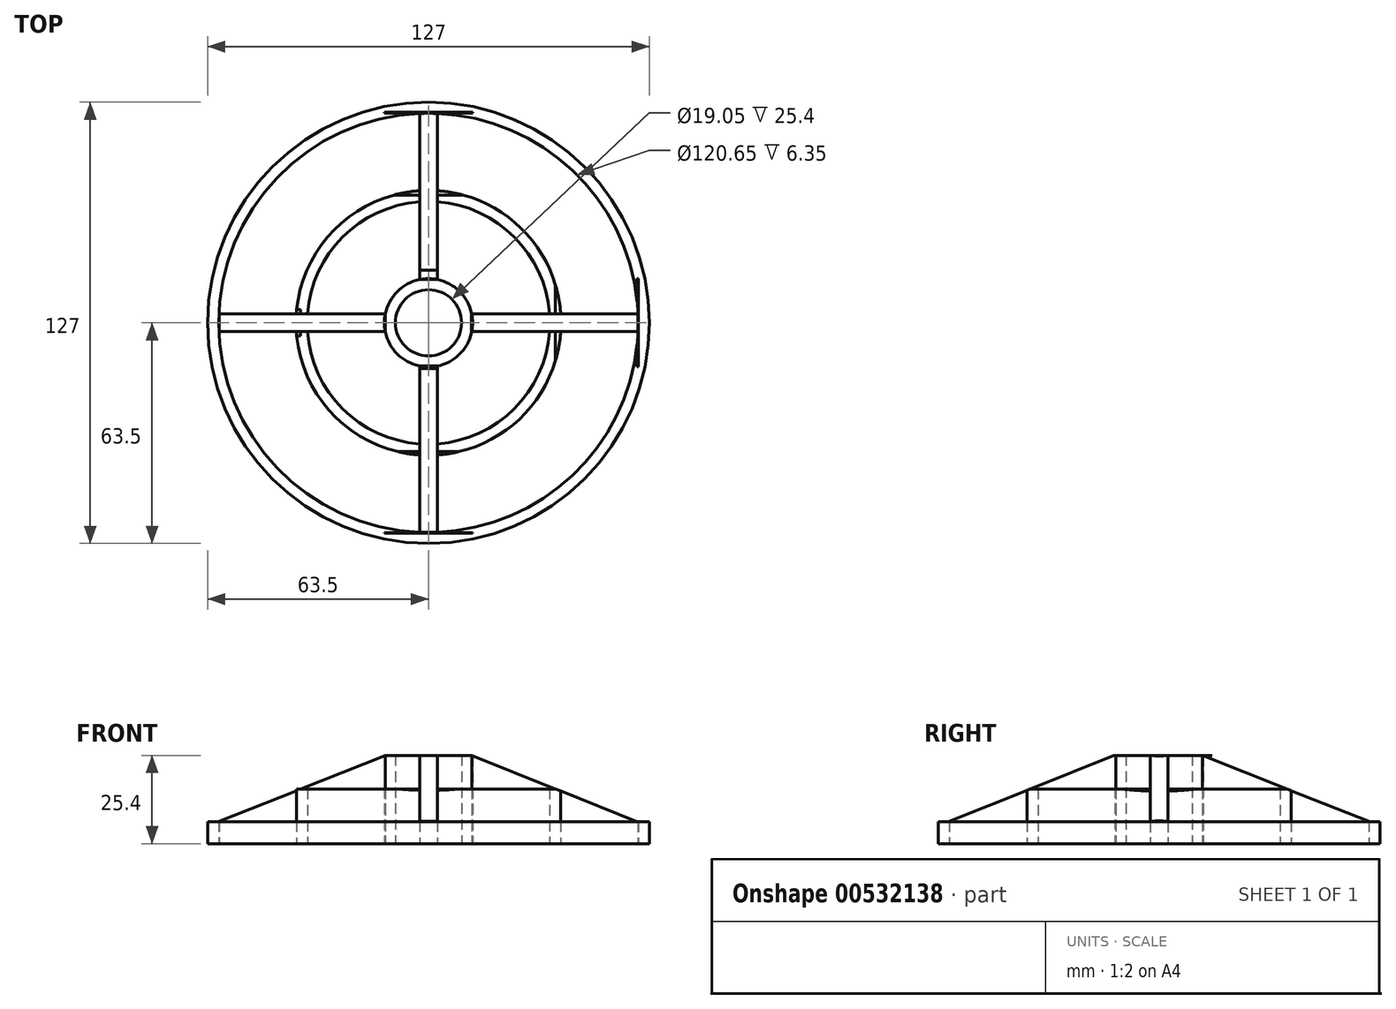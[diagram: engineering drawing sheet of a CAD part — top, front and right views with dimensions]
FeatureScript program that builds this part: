
annotation { "Feature Type Name" : "Feature", "Feature Type Description" : "" }
export const myFeature = defineFeature(function(context is Context, id is Id, definition is map)
    precondition{}
    {
        {
            var Q0;
            Q0=qCreatedBy(makeId("Top.planeOp"),FACE);
            var sketch = newSketch(context, id + "F0", { "sketchPlane" : qUnion([Q0])});
            skCircle(sketch, "E0", {"center": v(0, 0) * mm, "radius": 63.5 * mm});
            skCircle(sketch, "E1", {"center": v(0, 0) * mm, "radius": 38.1 * mm});
            skCircle(sketch, "E2", {"center": v(0, 0) * mm, "radius": 12.7 * mm});
            skLineSegment(sketch, "E3", {"start": v(-2.57, 63.45) * mm, "end": v(-2.57, 12.44) * mm});
            skLineSegment(sketch, "E4", {"start": v(2.51, 63.45) * mm, "end": v(2.51, 12.45) * mm});
            skLineSegment(sketch, "E5", {"start": v(-12.44, 2.55) * mm, "end": v(-63.45, 2.55) * mm});
            skLineSegment(sketch, "E6", {"start": v(-12.45, -2.53) * mm, "end": v(-63.45, -2.53) * mm});
            skLineSegment(sketch, "E7", {"start": v(2.51, -12.45) * mm, "end": v(2.51, -63.45) * mm});
            skLineSegment(sketch, "E8", {"start": v(-2.57, -12.44) * mm, "end": v(-2.57, -63.45) * mm});
            skLineSegment(sketch, "E9", {"start": v(12.44, 2.55) * mm, "end": v(63.45, 2.55) * mm});
            skLineSegment(sketch, "E10", {"start": v(12.45, -2.53) * mm, "end": v(63.45, -2.53) * mm});
            skCircle(sketch, "E11", {"center": v(0, 0) * mm, "radius": 60.33 * mm});
            skCircle(sketch, "E12", {"center": v(0, 0) * mm, "radius": 34.93 * mm});
            skCircle(sketch, "E13", {"center": v(0, 0) * mm, "radius": 9.53 * mm});
            skLineSegment(sketch, "E14", {"start": v(-60.21, 2.55) * mm, "end": v(-60.21, -2.53) * mm});
            skLineSegment(sketch, "E15", {"start": v(-12.44, 2.55) * mm, "end": v(-12.45, -2.53) * mm});
            skLineSegment(sketch, "E16", {"start": v(12.44, 2.55) * mm, "end": v(12.45, -2.53) * mm});
            skLineSegment(sketch, "E17", {"start": v(63.45, 2.55) * mm, "end": v(63.45, -2.53) * mm});
            skLineSegment(sketch, "E18", {"start": v(-2.57, 63.45) * mm, "end": v(2.51, 63.45) * mm});
            skLineSegment(sketch, "E19", {"start": v(2.51, 12.45) * mm, "end": v(-2.57, 12.44) * mm});
            skLineSegment(sketch, "E20", {"start": v(-2.57, -12.44) * mm, "end": v(2.51, -12.45) * mm});
            skLineSegment(sketch, "E21", {"start": v(2.51, -63.45) * mm, "end": v(-2.57, -63.45) * mm});
            skSolve(sketch);
        }
        {
            var Q0;
            Q0=qSketchRegion(id+"F0",true);
            extrude(context, id + "F1", {"entities" : qUnion([Q0]), "depth" : 6.35 * mm, "offsetDistance" : 25.4 * mm});
        }
        {
            var Q0;
            {var subQ0=sQuery(id+"F0.wireOp",EDGE,"E3");var subQ1=sQuery(id+"F0.wireOp",EDGE,"E1");var subQ2=makeQuery(id+"F0.imprint","INTERSECT",VERTEX,{"derivedFrom":[subQ1,subQ0]});Q0=makeQuery(id+"F0.imprint","IMPRINT",FACE,{"disambiguationData":[TD([[makeQuery(id+"F0.imprint","IMPRINT",EDGE,{"disambiguationData":[TD([[subQ2,-1.0]])],"derivedFrom":subQ1}),1.0]])]});}
            var Q1;
            {var subQ0=sQuery(id+"F0.wireOp",EDGE,"E4");var subQ1=sQuery(id+"F0.wireOp",EDGE,"E1");var subQ2=makeQuery(id+"F0.imprint","INTERSECT",VERTEX,{"derivedFrom":[subQ1,subQ0]});Q1=makeQuery(id+"F0.imprint","IMPRINT",FACE,{"disambiguationData":[TD([[makeQuery(id+"F0.imprint","IMPRINT",EDGE,{"disambiguationData":[TD([[subQ2,1.0]])],"derivedFrom":subQ1}),1.0]])]});}
            var Q2;
            {var subQ0=sQuery(id+"F0.wireOp",EDGE,"E7");var subQ1=sQuery(id+"F0.wireOp",EDGE,"E1");var subQ2=makeQuery(id+"F0.imprint","INTERSECT",VERTEX,{"derivedFrom":[subQ1,subQ0]});Q2=makeQuery(id+"F0.imprint","IMPRINT",FACE,{"disambiguationData":[TD([[makeQuery(id+"F0.imprint","IMPRINT",EDGE,{"disambiguationData":[TD([[subQ2,-1.0]])],"derivedFrom":subQ1}),1.0]])]});}
            var Q3;
            {var subQ0=sQuery(id+"F0.wireOp",EDGE,"E6");var subQ1=sQuery(id+"F0.wireOp",EDGE,"E1");var subQ2=makeQuery(id+"F0.imprint","INTERSECT",VERTEX,{"derivedFrom":[subQ1,subQ0]});Q3=makeQuery(id+"F0.imprint","IMPRINT",FACE,{"disambiguationData":[TD([[makeQuery(id+"F0.imprint","IMPRINT",EDGE,{"disambiguationData":[TD([[subQ2,-1.0]])],"derivedFrom":subQ1}),1.0]])]});}
            extrude(context, id + "F2", {"entities" : qUnion([Q0, Q1, Q2, Q3]), "depth" : 15.75 * mm, "offsetDistance" : 25.4 * mm});
        }
        {
            var Q0;
            {var subQ5=sQuery(id+"F0.wireOp",EDGE,"E14");Q0=makeQuery(id+"F0.imprint","IMPRINT",FACE,{"disambiguationData":[TD([[makeQuery(id+"F0.imprint","IMPRINT",EDGE,{"derivedFrom":subQ5}),1.0]])]});}
            var Q1;
            {var subQ0=sQuery(id+"F0.wireOp",EDGE,"E5");var subQ1=sQuery(id+"F0.wireOp",EDGE,"E1");var subQ2=makeQuery(id+"F0.imprint","INTERSECT",VERTEX,{"derivedFrom":[subQ1,subQ0]});Q1=makeQuery(id+"F0.imprint","IMPRINT",FACE,{"disambiguationData":[TD([[makeQuery(id+"F0.imprint","IMPRINT",EDGE,{"disambiguationData":[TD([[subQ2,-1.0]])],"derivedFrom":subQ1}),1.0]])]});}
            var Q2;
            {var subQ1=sQuery(id+"F0.wireOp",EDGE,"E5");var subQ6=sQuery(id+"F0.wireOp",EDGE,"E12");var subQ7=makeQuery(id+"F0.imprint","INTERSECT",VERTEX,{"derivedFrom":[subQ1,subQ6]});Q2=makeQuery(id+"F0.imprint","IMPRINT",FACE,{"disambiguationData":[TD([[makeQuery(id+"F0.imprint","IMPRINT",EDGE,{"disambiguationData":[TD([[subQ7,-1.0]])],"derivedFrom":subQ6}),1.0]])]});}
            extrude(context, id + "F3", {"entities" : qUnion([Q0, Q1, Q2]), "depth" : 25.4 * mm, "offsetDistance" : 25.4 * mm});
        }
        {
            var Q0;
            Q0=makeQuery(id+"F0.imprint","IMPRINT",FACE,{"disambiguationData":[TD([[makeQuery(id+"F0.imprint","IMPRINT",EDGE,{"derivedFrom":sQuery(id+"F0.wireOp",EDGE,"E13")}),-1.0]])]});
            extrude(context, id + "F4", {"entities" : qUnion([Q0]), "depth" : 25.4 * mm, "offsetDistance" : 25.4 * mm});
        }
        {
            var Q0;
            {var subQ1=sQuery(id+"F0.wireOp",EDGE,"E3");var subQ6=sQuery(id+"F0.wireOp",EDGE,"E12");var subQ7=makeQuery(id+"F0.imprint","INTERSECT",VERTEX,{"derivedFrom":[subQ1,subQ6]});Q0=makeQuery(id+"F0.imprint","IMPRINT",FACE,{"disambiguationData":[TD([[makeQuery(id+"F0.imprint","IMPRINT",EDGE,{"disambiguationData":[TD([[subQ7,1.0]])],"derivedFrom":subQ6}),1.0]])]});}
            var Q1;
            {var subQ0=sQuery(id+"F0.wireOp",EDGE,"E4");var subQ1=sQuery(id+"F0.wireOp",EDGE,"E1");var subQ2=makeQuery(id+"F0.imprint","INTERSECT",VERTEX,{"derivedFrom":[subQ1,subQ0]});Q1=makeQuery(id+"F0.imprint","IMPRINT",FACE,{"disambiguationData":[TD([[makeQuery(id+"F0.imprint","IMPRINT",EDGE,{"disambiguationData":[TD([[subQ2,-1.0]])],"derivedFrom":subQ1}),1.0]])]});}
            var Q2;
            {var subQ0=sQuery(id+"F0.wireOp",EDGE,"E4");var subQ1=sQuery(id+"F0.wireOp",EDGE,"E1");var subQ2=makeQuery(id+"F0.imprint","INTERSECT",VERTEX,{"derivedFrom":[subQ1,subQ0]});Q2=makeQuery(id+"F0.imprint","IMPRINT",FACE,{"disambiguationData":[TD([[makeQuery(id+"F0.imprint","IMPRINT",EDGE,{"disambiguationData":[TD([[subQ2,-1.0]])],"derivedFrom":subQ1}),-1.0]])]});}
            extrude(context, id + "F5", {"entities" : qUnion([Q0, Q1, Q2]), "depth" : 25.4 * mm, "offsetDistance" : 25.4 * mm});
        }
        {
            var Q0;
            {var subQ1=sQuery(id+"F0.wireOp",EDGE,"E9");var subQ6=sQuery(id+"F0.wireOp",EDGE,"E12");var subQ7=makeQuery(id+"F0.imprint","INTERSECT",VERTEX,{"derivedFrom":[subQ1,subQ6]});Q0=makeQuery(id+"F0.imprint","IMPRINT",FACE,{"disambiguationData":[TD([[makeQuery(id+"F0.imprint","IMPRINT",EDGE,{"disambiguationData":[TD([[subQ7,1.0]])],"derivedFrom":subQ6}),1.0]])]});}
            var Q1;
            {var subQ0=sQuery(id+"F0.wireOp",EDGE,"E9");var subQ1=sQuery(id+"F0.wireOp",EDGE,"E1");var subQ2=makeQuery(id+"F0.imprint","INTERSECT",VERTEX,{"derivedFrom":[subQ1,subQ0]});Q1=makeQuery(id+"F0.imprint","IMPRINT",FACE,{"disambiguationData":[TD([[makeQuery(id+"F0.imprint","IMPRINT",EDGE,{"disambiguationData":[TD([[subQ2,1.0]])],"derivedFrom":subQ1}),1.0]])]});}
            var Q2;
            {var subQ0=sQuery(id+"F0.wireOp",EDGE,"E9");var subQ1=sQuery(id+"F0.wireOp",EDGE,"E1");var subQ2=makeQuery(id+"F0.imprint","INTERSECT",VERTEX,{"derivedFrom":[subQ1,subQ0]});Q2=makeQuery(id+"F0.imprint","IMPRINT",FACE,{"disambiguationData":[TD([[makeQuery(id+"F0.imprint","IMPRINT",EDGE,{"disambiguationData":[TD([[subQ2,1.0]])],"derivedFrom":subQ1}),-1.0]])]});}
            var Q3;
            {var subQ1=sQuery(id+"F0.wireOp",EDGE,"E7");var subQ6=sQuery(id+"F0.wireOp",EDGE,"E12");var subQ8=makeQuery(id+"F0.imprint","INTERSECT",VERTEX,{"derivedFrom":[subQ1,subQ6]});Q3=makeQuery(id+"F0.imprint","IMPRINT",FACE,{"disambiguationData":[TD([[makeQuery(id+"F0.imprint","IMPRINT",EDGE,{"disambiguationData":[TD([[subQ8,1.0]])],"derivedFrom":subQ6}),1.0]])]});}
            var Q4;
            {var subQ0=sQuery(id+"F0.wireOp",EDGE,"E8");var subQ1=sQuery(id+"F0.wireOp",EDGE,"E1");var subQ2=makeQuery(id+"F0.imprint","INTERSECT",VERTEX,{"derivedFrom":[subQ1,subQ0]});Q4=makeQuery(id+"F0.imprint","IMPRINT",FACE,{"disambiguationData":[TD([[makeQuery(id+"F0.imprint","IMPRINT",EDGE,{"disambiguationData":[TD([[subQ2,-1.0]])],"derivedFrom":subQ1}),1.0]])]});}
            var Q5;
            {var subQ0=sQuery(id+"F0.wireOp",EDGE,"E8");var subQ1=sQuery(id+"F0.wireOp",EDGE,"E1");var subQ2=makeQuery(id+"F0.imprint","INTERSECT",VERTEX,{"derivedFrom":[subQ1,subQ0]});Q5=makeQuery(id+"F0.imprint","IMPRINT",FACE,{"disambiguationData":[TD([[makeQuery(id+"F0.imprint","IMPRINT",EDGE,{"disambiguationData":[TD([[subQ2,-1.0]])],"derivedFrom":subQ1}),-1.0]])]});}
            extrude(context, id + "F6", {"entities" : qUnion([Q0, Q1, Q2, Q3, Q4, Q5]), "depth" : 25.4 * mm, "offsetDistance" : 25.4 * mm});
        }
        {
            var Q0;
            Q0=qCreatedBy(makeId("Front.planeOp"),FACE);
            var sketch = newSketch(context, id + "F7", { "sketchPlane" : qUnion([Q0])});
            skLineSegment(sketch, "E22", {"start": v(-60.26, 6.42) * mm, "end": v(-12.44, 25.4) * mm});
            skLineSegment(sketch, "E23", {"start": v(-12.44, 25.4) * mm, "end": v(-60.32, 25.4) * mm});
            skLineSegment(sketch, "E24", {"start": v(-60.32, 25.4) * mm, "end": v(-60.26, 6.42) * mm});
            skSolve(sketch);
        }
        {
            var Q0;
            Q0=qSketchRegion(id+"F7",true);
            extrude(context, id + "F8", {"entities" : qUnion([Q0]), "operationType" : NewBodyOperationType.REMOVE, "endBound" : BoundingType.SYMMETRIC, "oppositeDirection" : true, "depth" : 7.62 * mm, "offsetDistance" : 25.4 * mm});
        }
        {
            var Q0;
            Q0=qCreatedBy(makeId("Right.planeOp"),FACE);
            var sketch = newSketch(context, id + "F9", { "sketchPlane" : qUnion([Q0])});
            skLineSegment(sketch, "E25", {"start": v(-12.14, 25.8) * mm, "end": v(-60.52, 6.3) * mm});
            skLineSegment(sketch, "E26", {"start": v(-60.52, 6.3) * mm, "end": v(-60.52, 26.22) * mm});
            skLineSegment(sketch, "E27", {"start": v(-60.52, 26.22) * mm, "end": v(-12.14, 25.8) * mm});
            skSolve(sketch);
        }
        {
            var Q0;
            Q0=qSketchRegion(id+"F9",true);
            extrude(context, id + "F10", {"entities" : qUnion([Q0]), "operationType" : NewBodyOperationType.REMOVE, "endBound" : BoundingType.SYMMETRIC, "oppositeDirection" : true, "depth" : 25.4 * mm, "offsetDistance" : 25.4 * mm});
        }
        {
            var Q0;
            Q0=qCreatedBy(makeId("Right.planeOp"),FACE);
            var sketch = newSketch(context, id + "F11", { "sketchPlane" : qUnion([Q0])});
            skLineSegment(sketch, "E28", {"start": v(12.58, 25.38) * mm, "end": v(60.67, 6.24) * mm});
            skLineSegment(sketch, "E29", {"start": v(60.67, 6.24) * mm, "end": v(60.67, 25.8) * mm});
            skLineSegment(sketch, "E30", {"start": v(60.67, 25.8) * mm, "end": v(12.58, 25.38) * mm});
            skSolve(sketch);
        }
        {
            var Q0;
            Q0=qSketchRegion(id+"F11",true);
            extrude(context, id + "F12", {"entities" : qUnion([Q0]), "operationType" : NewBodyOperationType.REMOVE, "endBound" : BoundingType.SYMMETRIC, "oppositeDirection" : true, "depth" : 25.4 * mm, "offsetDistance" : 25.4 * mm});
        }
        {
            var Q0;
            Q0=qCreatedBy(makeId("Front.planeOp"),FACE);
            var sketch = newSketch(context, id + "F13", { "sketchPlane" : qUnion([Q0])});
            skLineSegment(sketch, "E31", {"start": v(12.36, 25.4) * mm, "end": v(60.27, 6.25) * mm});
            skLineSegment(sketch, "E32", {"start": v(60.27, 25.66) * mm, "end": v(12.36, 25.4) * mm});
            skLineSegment(sketch, "E33", {"start": v(61.52, 12.59) * mm, "end": v(60.27, 6.25) * mm});
            skLineSegment(sketch, "E34", {"start": v(60.27, 25.66) * mm, "end": v(63.44, 24.97) * mm});
            skLineSegment(sketch, "E35", {"start": v(63.44, 24.97) * mm, "end": v(61.52, 12.59) * mm});
            skSolve(sketch);
        }
        {
            var Q0;
            Q0=qSketchRegion(id+"F13",true);
            extrude(context, id + "F14", {"entities" : qUnion([Q0]), "operationType" : NewBodyOperationType.REMOVE, "endBound" : BoundingType.SYMMETRIC, "oppositeDirection" : true, "depth" : 25.4 * mm, "offsetDistance" : 25.4 * mm});
        }
    });
